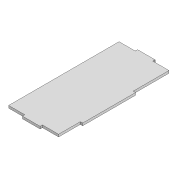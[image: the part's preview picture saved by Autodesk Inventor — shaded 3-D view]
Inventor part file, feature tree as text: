
AUTODESK INVENTOR PART (.ipt)
format: ipt  version: 2021 (Build 250183000, 183)  size: 119,296 bytes
history: native  units: mm
features: other x1, extrude x1, sketch x1
ambient origin geometry x8: Origin, YZ Plane, XZ Plane, XY Plane, X Axis, Y Axis, Z Axis, Center Point
bodies: Body1 (feature_tree)
feature tree (3):
  other  "Твердое тело1"
  extrude  "Выдавливание1"  Depth=4.0mm TaperAngle=0.0deg
  sketch  "Эскиз1"
